# Revit family: Naughtone_Stng_Hatch
name_source: partatom
category: Furniture
revit_build: Autodesk Revit 2015 (Build: 20160512_1515(x64)
units: mm (PartAtom-declared; Revit-internal decimal feet)

## types (11) — shared parameters
Assembly Code = E2020200
AssetType = Moveable
BIMObjectName = Naughtone_Seating_Hatch
Category = Pr_40_50_12: Chairs, seats and benches
CodePerformance = PASSED BSEN 16139
Color = Various
DurationUnit = year
Finish = Upholstered
IfcExportAs = IfcFurnishingElementType
Keynote = Pr_40_50_12
MainColor = Various
ManufacturerAddressUK = naughtone, Knaresborough Tech Park, Manse Lane, Knaresborough, HG5 8LF
ManufacturerName = Naughtone
ManufacturerURL = www.naughtone.com
Material = Fabric, leather/steel/solid wood/beech ply/foam
NBSDescription = Seating
NBSReference = 45-35-72/352
Name = Seating_Hatch_Naughtone
NominalHeight = 685 mm  [stored 2.24738 ft]
NominalWidth = 690 mm  [stored 2.26378 ft]
ProductInformation = www.naughtone.com/portfolio-view/hatch
SustainabilityPerformance = FSC certified. FISP certified. ISO 14001 certified
URL = www.naughtone.com
Uniclass2015Description = Chairs, seats and benches
Uniclass2015Reference = Pr_40_50_12
Uniclass2015Version = Products v1.5
Version = 1
WarrantyDurationLabor = 5
WarrantyDurationParts = 5
WarrantyDurationUnit = year

## per-type parameters (varying)
| type | Description | HasNoArms | HasOneArmL | HasOneArmR | HasTwoArms | IfcExportType | Is2Seat | Is3Seat | IsChair | LeftOffset | ModelReference | RightOffset | Shape | Size | VoidOffset2Seat | VoidOffset3Seat | VoidOffsetCentre |
| HAT1NA | Hatch Chair No Arms | Yes | No | No | No | SOFA | No | No | No | 255 mm  [stored 0.836614 ft] | Hatch Chair No Arms | 255 mm  [stored 0.836614 ft] | Rectangular | 510x690x685mm | 10 mm  [stored 0.0328084 ft] | 10 mm  [stored 0.0328084 ft] | 255 mm  [stored 0.836614 ft] |
| HAT11A | Hatch Corner Chair 1 Arm | No | Yes | No | No | SOFA | No | No | Yes | 255 mm  [stored 0.836614 ft] | Hatch Corner Chair 1 Arm | 255 mm  [stored 0.836614 ft] | Square | 690x690x685mm | 10 mm  [stored 0.0328084 ft] | 10 mm  [stored 0.0328084 ft] | 255 mm  [stored 0.836614 ft] |
| HAT12A | Hatch Chair 2 Arms | No | No | No | Yes | CHAIR | No | No | No | 255 mm  [stored 0.836614 ft] | Hatch Chair 2 Arms | 255 mm  [stored 0.836614 ft] | Rectangular | 870x690x685mm | 10 mm  [stored 0.0328084 ft] | 10 mm  [stored 0.0328084 ft] | 255 mm  [stored 0.836614 ft] |
| HAT2NA | Hatch 2 Seater No Arms | Yes | No | No | No | SOFA | Yes | No | Yes | 510 mm  [stored 1.67323 ft] | Hatch 2 Seater No Arms | 510 mm  [stored 1.67323 ft] | Rectangular | 1020x690x685mm | 0 mm  [stored 0 ft] | 10 mm  [stored 0.0328084 ft] | 0 mm  [stored 0 ft] |
| HAT2RA | Hatch 2 Seater Right Arm | No | No | Yes | No | SOFA | Yes | No | Yes | 510 mm  [stored 1.67323 ft] | Hatch 2 Seater Right Arm | 510 mm  [stored 1.67323 ft] | Rectangular | 1200x690x685mm | 0 mm  [stored 0 ft] | 10 mm  [stored 0.0328084 ft] | 0 mm  [stored 0 ft] |
| HAT2LA | Hatch 2 Seater Left Arm | No | Yes | No | No | SOFA | Yes | No | Yes | 510 mm  [stored 1.67323 ft] | Hatch 2 Seater Left Arm | 510 mm  [stored 1.67323 ft] | Rectangular | 1200x690x685mm | 0 mm  [stored 0 ft] | 10 mm  [stored 0.0328084 ft] | 0 mm  [stored 0 ft] |
| HAT22A | Hatch 2 Seater 2 Arms | No | No | No | Yes | SOFA | Yes | No | Yes | 510 mm  [stored 1.67323 ft] | Hatch 2 Seater 2 Arms | 510 mm  [stored 1.67323 ft] | Rectangular | 1380x690x685mm | 0 mm  [stored 0 ft] | 10 mm  [stored 0.0328084 ft] | 0 mm  [stored 0 ft] |
| HAT3NA | Hatch 3 Seater No Arms | Yes | No | No | No | SOFA | Yes | Yes | No | 765 mm  [stored 2.50984 ft] | Hatch 3 Seater No Arms | 765 mm  [stored 2.50984 ft] | Rectangular | 1530x690x685mm | 0 mm  [stored 0 ft] | 0 mm  [stored 0 ft] | 255 mm  [stored 0.836614 ft] |
| HAT3RA | Hatch 3 Seater Right Arm | No | No | Yes | No | SOFA | Yes | Yes | No | 765 mm  [stored 2.50984 ft] | Hatch 3 Seater Right Arm | 765 mm  [stored 2.50984 ft] | Rectangular | 1710x690x685mm | 0 mm  [stored 0 ft] | 0 mm  [stored 0 ft] | 255 mm  [stored 0.836614 ft] |
| HAT3LA | Hatch 3 Seater Left Arm | No | Yes | No | No | SOFA | Yes | Yes | No | 765 mm  [stored 2.50984 ft] | Hatch 3 Seater Left Arm | 765 mm  [stored 2.50984 ft] | Rectangular | 1710x690x685mm | 0 mm  [stored 0 ft] | 0 mm  [stored 0 ft] | 255 mm  [stored 0.836614 ft] |
| HAT32A | Hatch 3 Seater 2 Arms | No | No | No | Yes | SOFA | Yes | Yes | No | 765 mm  [stored 2.50984 ft] | Hatch 3 Seater 2 Arms | 765 mm  [stored 2.50984 ft] | Rectangular | 1890x690x685mm | 0 mm  [stored 0 ft] | 0 mm  [stored 0 ft] | 255 mm  [stored 0.836614 ft] |

note: column(s) folded — value = type name in every type: Model, ModelNumber

note: [stored X ft] marks values corroborated as IEEE doubles in the binary element streams (Revit-internal decimal feet)

## geometry (parser evidence)
native form markers: Sweep x2
no freeform markers — native parametric forms only
